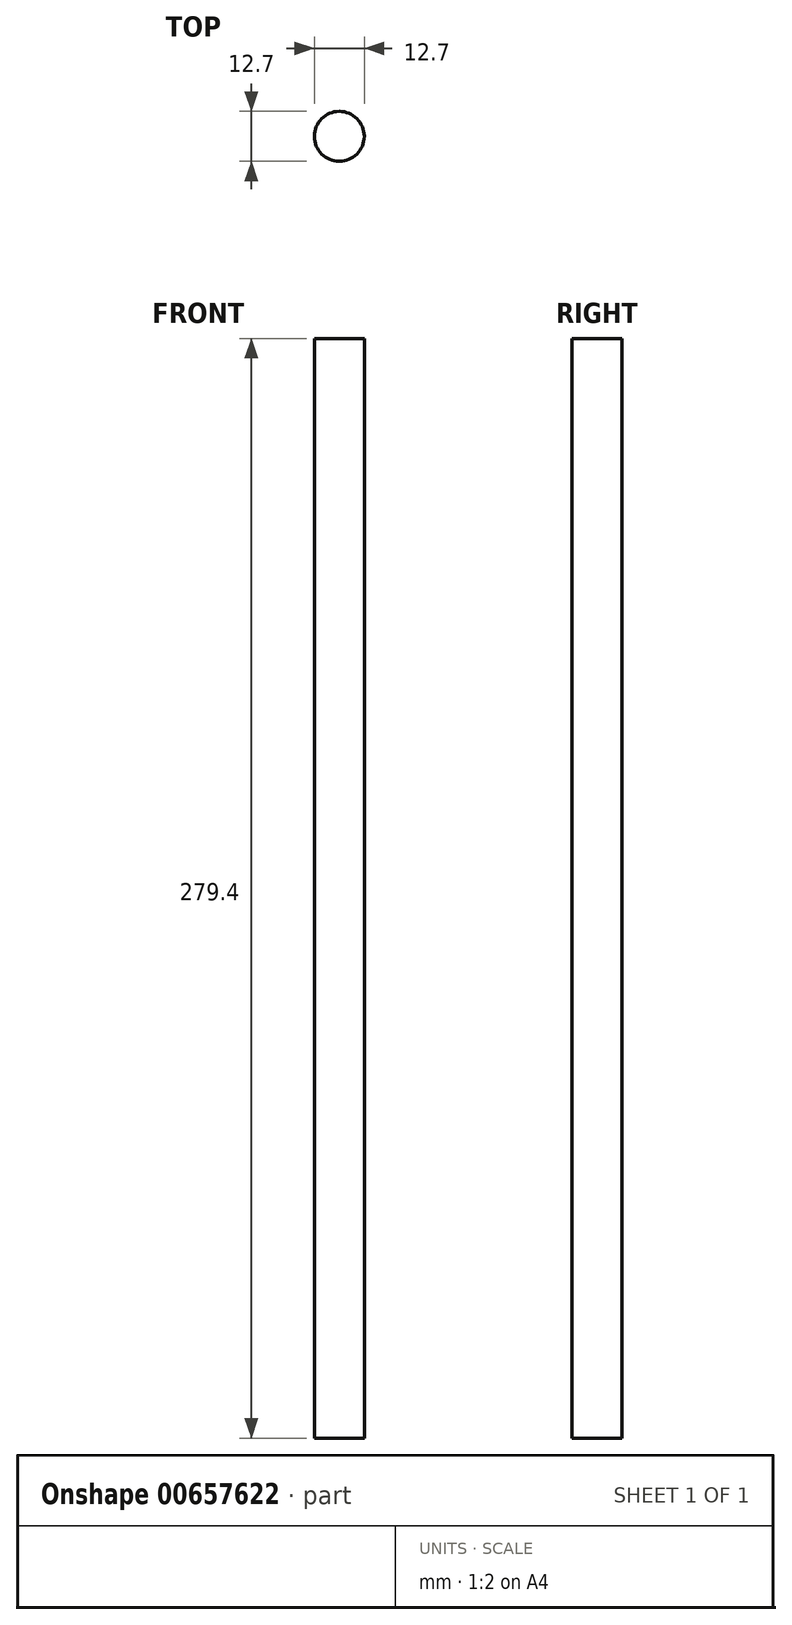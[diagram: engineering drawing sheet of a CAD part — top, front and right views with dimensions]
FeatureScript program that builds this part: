
annotation { "Feature Type Name" : "Feature", "Feature Type Description" : "" }
export const myFeature = defineFeature(function(context is Context, id is Id, definition is map)
    precondition{}
    {
        {
            var Q0;
            Q0=qCreatedBy(makeId("Top.planeOp"),FACE);
            var sketch = newSketch(context, id + "F0", { "sketchPlane" : qUnion([Q0])});
            skCircle(sketch, "E0", {"center": v(0, 0) * mm, "radius": 6.35 * mm});
            skSolve(sketch);
        }
        {
            var Q0;
            Q0=makeQuery(id+"F0.imprint","IMPRINT",FACE,{"disambiguationData":[TD([[makeQuery(id+"F0.imprint","IMPRINT",EDGE,{"derivedFrom":sQuery(id+"F0.wireOp",EDGE,"E0")}),1.0]])]});
            extrude(context, id + "F1", {"entities" : qUnion([Q0]), "depth" : 279.4 * mm, "offsetDistance" : 25.4 * mm});
        }
    });
